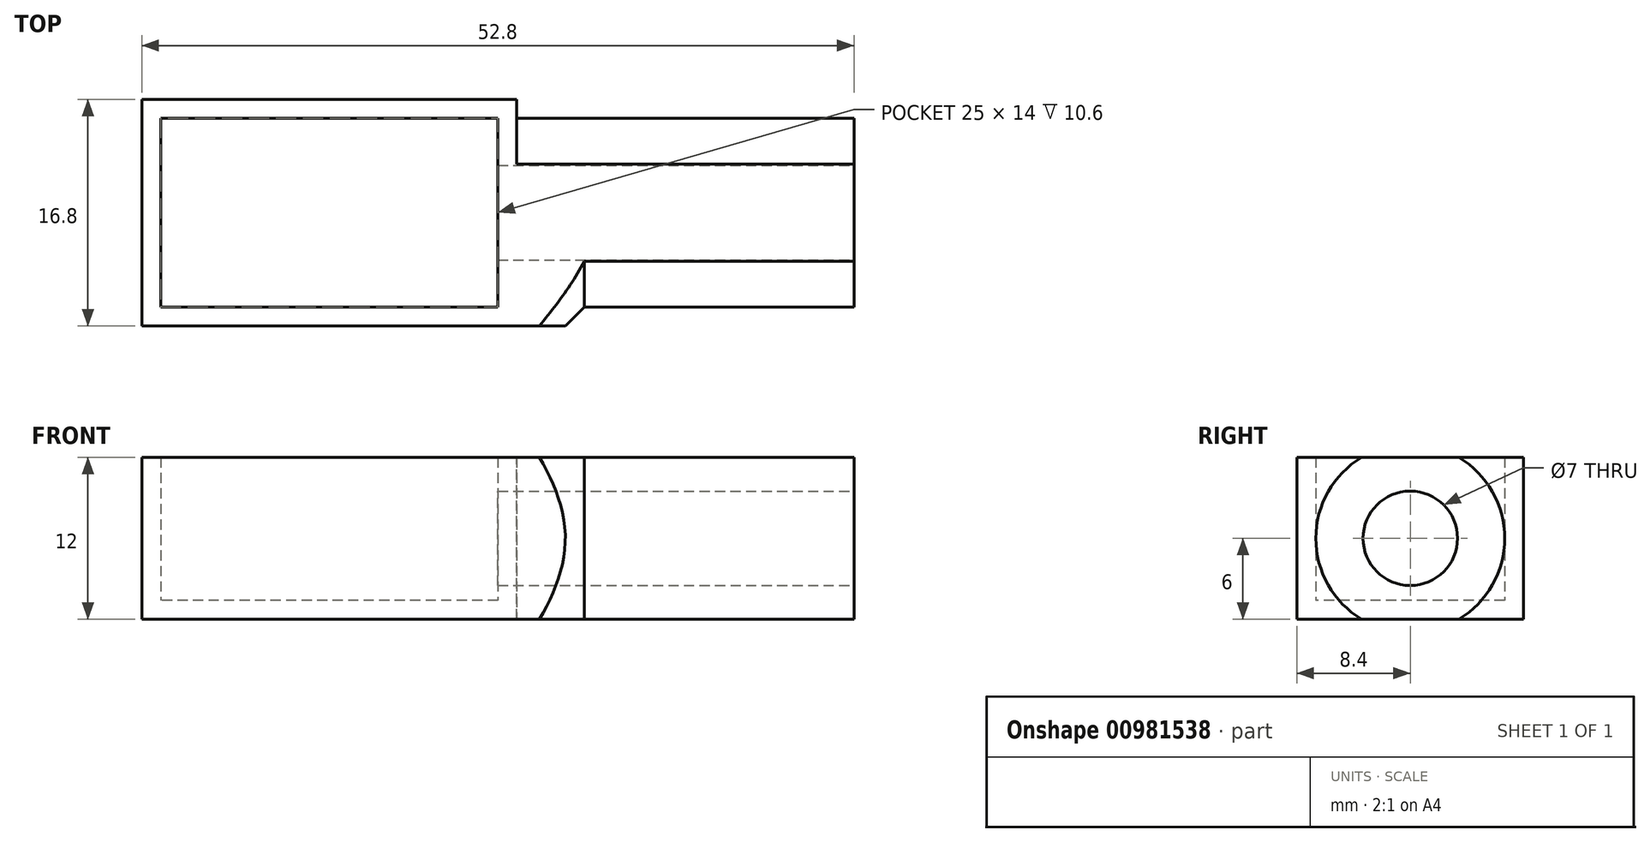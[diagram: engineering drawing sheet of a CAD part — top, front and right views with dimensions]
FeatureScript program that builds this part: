
annotation { "Feature Type Name" : "Feature", "Feature Type Description" : "" }
export const myFeature = defineFeature(function(context is Context, id is Id, definition is map)
    precondition{}
    {
        {
            var Q0;
            Q0=qCreatedBy(makeId("Top.planeOp"),FACE);
            var sketch = newSketch(context, id + "F0", { "sketchPlane" : qUnion([Q0])});
            skLineSegment(sketch, "E0.bottom", {"start": v(12.5, 7) * mm, "end": v(-12.5, 7) * mm});
            skLineSegment(sketch, "E0.top", {"start": v(12.5, -7) * mm, "end": v(-12.5, -7) * mm});
            skLineSegment(sketch, "E0.left", {"start": v(12.5, 7) * mm, "end": v(12.5, -7) * mm});
            skLineSegment(sketch, "E0.right", {"start": v(-12.5, 7) * mm, "end": v(-12.5, -7) * mm});
            skPoint(sketch, "E0.middle", {"position": v(0, 0) * mm});
            skLineSegment(sketch, "E1.0", {"start": v(13.9, 8.4) * mm, "end": v(-13.9, 8.4) * mm});
            skLineSegment(sketch, "E1.1", {"start": v(13.9, 8.4) * mm, "end": v(13.9, -8.4) * mm});
            skLineSegment(sketch, "E1.2", {"start": v(13.9, -8.4) * mm, "end": v(-13.9, -8.4) * mm});
            skLineSegment(sketch, "E1.3", {"start": v(-13.9, 8.4) * mm, "end": v(-13.9, -8.4) * mm});
            skLineSegment(sketch, "E2", {"start": v(12.5, -7) * mm, "end": v(13.9, -7) * mm});
            skLineSegment(sketch, "E3", {"start": v(12.5, 7) * mm, "end": v(13.9, 7) * mm});
            skSolve(sketch);
        }
        {
            var Q0;
            Q0 = qSketchRegion(id + "F0", true);
            extrude(context, id + "F1", {"entities" : qUnion([Q0]), "depth" : 12 * mm, "offsetDistance" : 25 * mm});
        }
        {
            var Q0;
            Q0=makeQuery(id+"F0.imprint","IMPRINT",FACE,{"disambiguationData":[TD([[makeQuery(id+"F0.imprint","IMPRINT",EDGE,{"derivedFrom":sQuery(id+"F0.wireOp",EDGE,"E0.bottom")}),1.0]])]});
            extrude(context, id + "F2", {"entities" : qUnion([Q0]), "operationType" : NewBodyOperationType.ADD, "depth" : 1.4 * mm, "offsetDistance" : 25 * mm});
        }
        {
            var Q0;
            Q0=makeQuery(id+"F1.opExtrude","SWEPT_FACE",FACE,{"disambiguationData":[OSD([sQuery(id+"F0.wireOp",EDGE,"E1.1")])]});
            var sketch = newSketch(context, id + "F3", { "sketchPlane" : qUnion([Q0])});
            skCircle(sketch, "E4", {"center": v(0, 6) * mm, "radius": 7 * mm});
            skCircle(sketch, "E5.0", {"center": v(0, 6) * mm, "radius": 3.5 * mm});
            skLineSegment(sketch, "E6", {"start": v(3.6, 0) * mm, "end": v(3.6, 0) * mm});
            skLineSegment(sketch, "E7", {"start": v(-3.6, 12) * mm, "end": v(3.6, 12) * mm});
            skSolve(sketch);
        }
        {
            var Q0;
            Q0=makeQuery(id+"F3.imprint","IMPRINT",FACE,{"disambiguationData":[TD([[makeQuery(id+"F3.imprint","IMPRINT",EDGE,{"derivedFrom":sQuery(id+"F3.wireOp",EDGE,"E5.0")}),1.0]])]});
            var Q1;
            Q1=makeQuery(id+"F1.opExtrude","SWEPT_FACE",FACE,{"disambiguationData":[OSD([sQuery(id+"F0.wireOp",EDGE,"E0.left")])]});
            extrude(context, id + "F4", {"entities" : qUnion([Q0]), "operationType" : NewBodyOperationType.REMOVE, "endBound" : BoundingType.UP_TO_SURFACE, "oppositeDirection" : true, "depth" : 25 * mm, "endBoundEntityFace" : qUnion([Q1]), "offsetDistance" : 25 * mm});
        }
        {
            var Q0;
            Q0=makeQuery(id+"F3.imprint","IMPRINT",FACE,{"disambiguationData":[TD([[makeQuery(id+"F3.imprint","IMPRINT",EDGE,{"derivedFrom":sQuery(id+"F3.wireOp",EDGE,"E5.0")}),-1.0]])]});
            extrude(context, id + "F5", {"entities" : qUnion([Q0]), "operationType" : NewBodyOperationType.ADD, "depth" : 25 * mm, "offsetDistance" : 25 * mm});
        }
        {
            var Q0;
            Q0=makeQuery(id+"F5.opExtrude","CAP_EDGE",EDGE,{"disambiguationData":[OSD([sQuery(id+"F3.wireOp",EDGE,"E4")])],"isStart":true});
            chamfer(context, id + "F6", {"entities" : qUnion([Q0]), "width" : 5 * mm, "tangentPropagation" : true});
        }
    });
